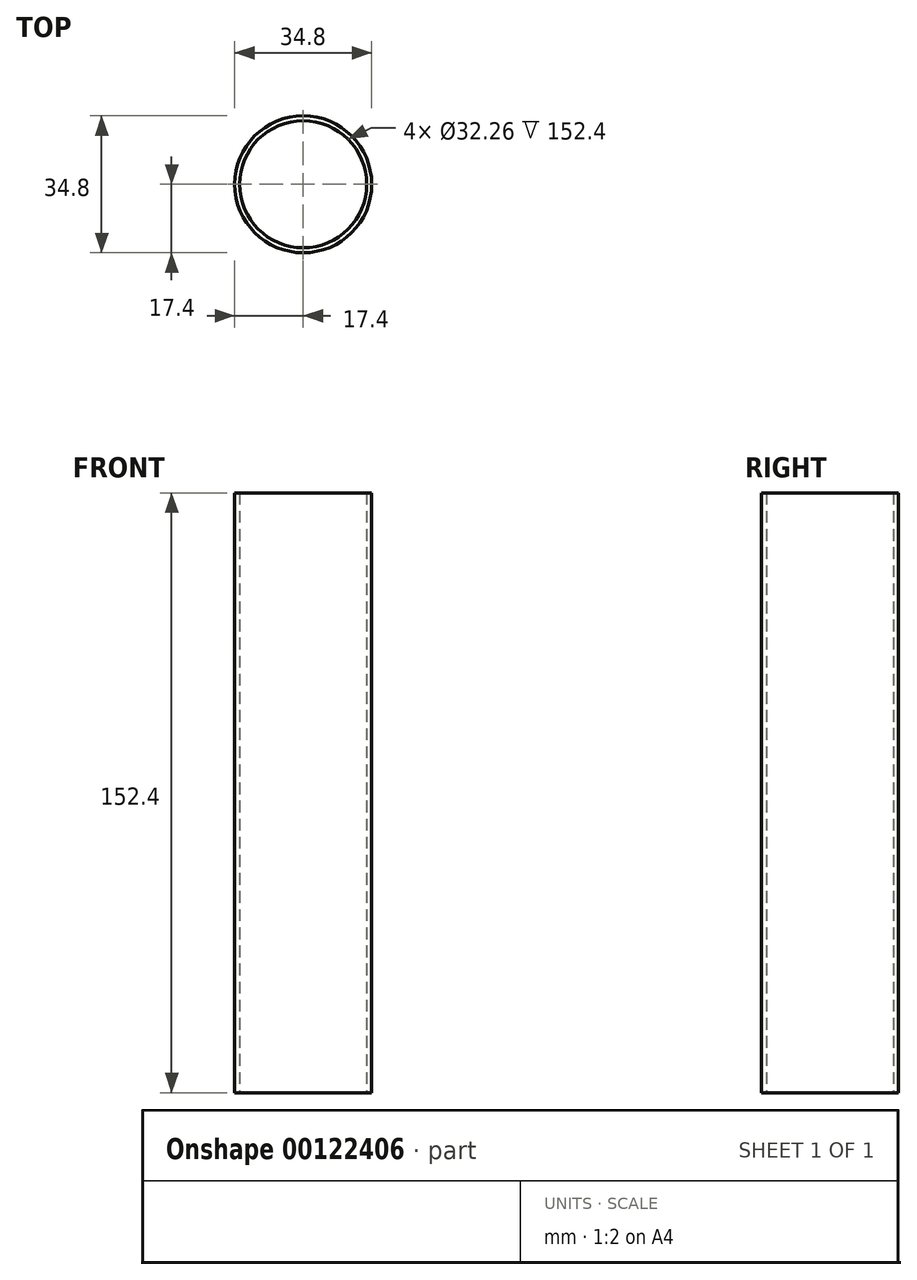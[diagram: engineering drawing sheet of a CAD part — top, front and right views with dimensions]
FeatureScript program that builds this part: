
annotation { "Feature Type Name" : "Feature", "Feature Type Description" : "" }
export const myFeature = defineFeature(function(context is Context, id is Id, definition is map)
    precondition{}
    {
        {
            var Q0;
            Q0=qCreatedBy(makeId("Top.planeOp"),FACE);
            var sketch = newSketch(context, id + "F0", { "sketchPlane" : qUnion([Q0])});
            skCircle(sketch, "E0", {"center": v(0, 0) * mm, "radius": 17.4 * mm});
            skCircle(sketch, "E1", {"center": v(0, 0) * mm, "radius": 16.13 * mm});
            skSolve(sketch);
        }
        {
            var Q0;
            Q0 = qSketchRegion(id + "F0", true);
            extrude(context, id + "F1", {"entities" : qUnion([Q0]), "depth" : 152.4 * mm});
        }
    });
